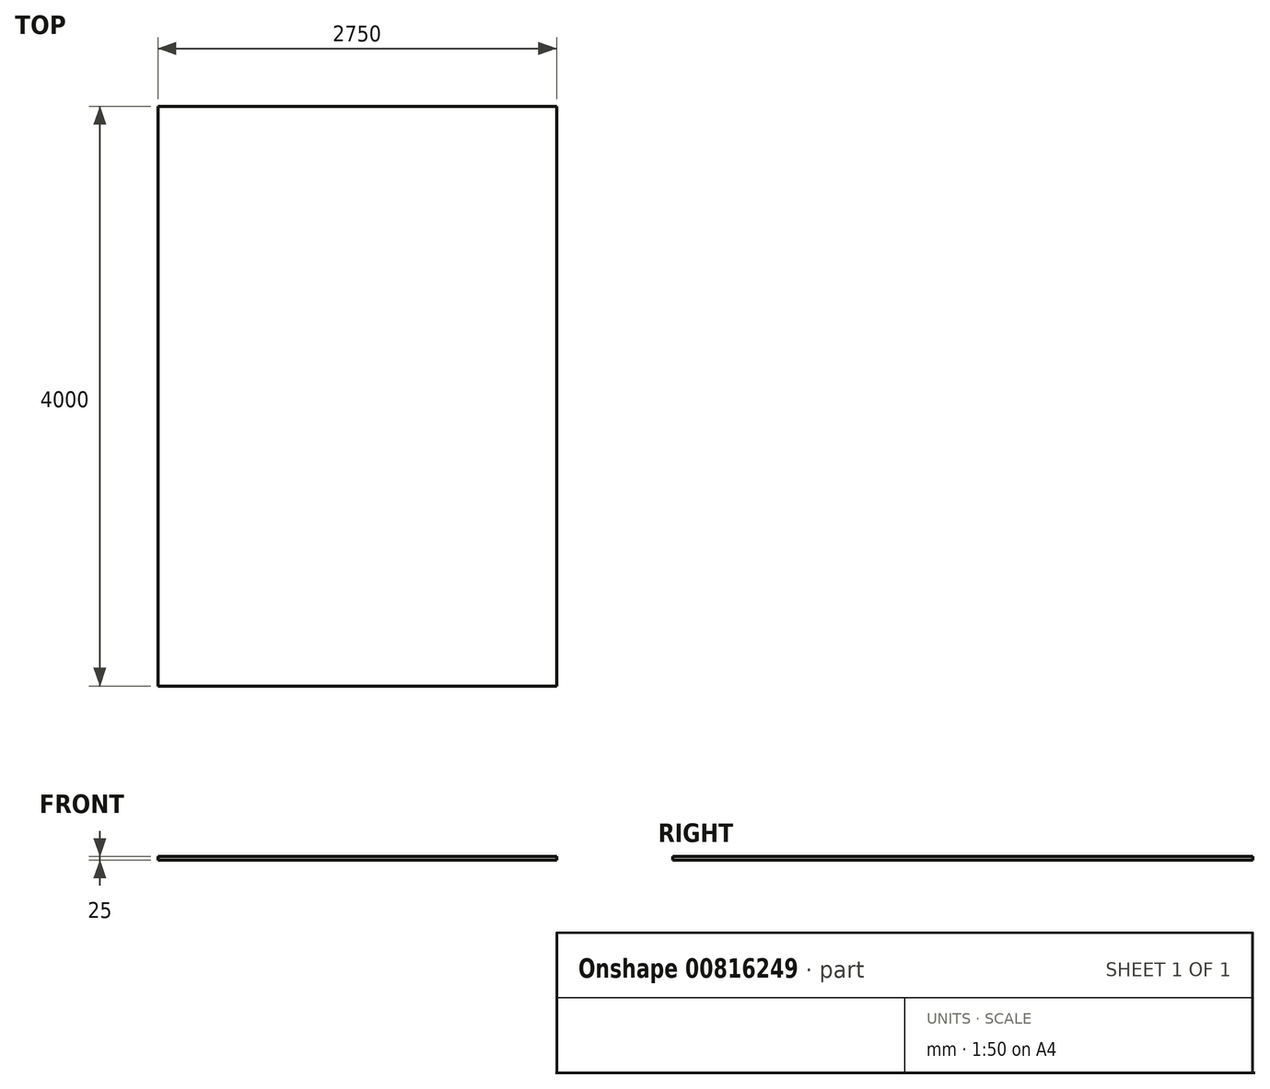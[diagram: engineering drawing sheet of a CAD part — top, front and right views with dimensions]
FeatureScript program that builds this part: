
annotation { "Feature Type Name" : "Feature", "Feature Type Description" : "" }
export const myFeature = defineFeature(function(context is Context, id is Id, definition is map)
    precondition{}
    {
        {
            var Q0;
            Q0=qCreatedBy(makeId("Top.planeOp"),FACE);
            var sketch = newSketch(context, id + "F0", { "sketchPlane" : qUnion([Q0])});
            skLineSegment(sketch, "E0.bottom", {"start": v(0, 0) * mm, "end": v(2750, 0) * mm});
            skLineSegment(sketch, "E0.top", {"start": v(0, 4000) * mm, "end": v(2750, 4000) * mm});
            skLineSegment(sketch, "E0.left", {"start": v(0, 0) * mm, "end": v(0, 4000) * mm});
            skLineSegment(sketch, "E0.right", {"start": v(2750, 0) * mm, "end": v(2750, 4000) * mm});
            skSolve(sketch);
        }
        {
            var Q0;
            Q0 = qSketchRegion(id + "F0", true);
            extrude(context, id + "F1", {"entities" : qUnion([Q0]), "depth" : 25 * mm, "offsetDistance" : 25 * mm});
        }
    });
